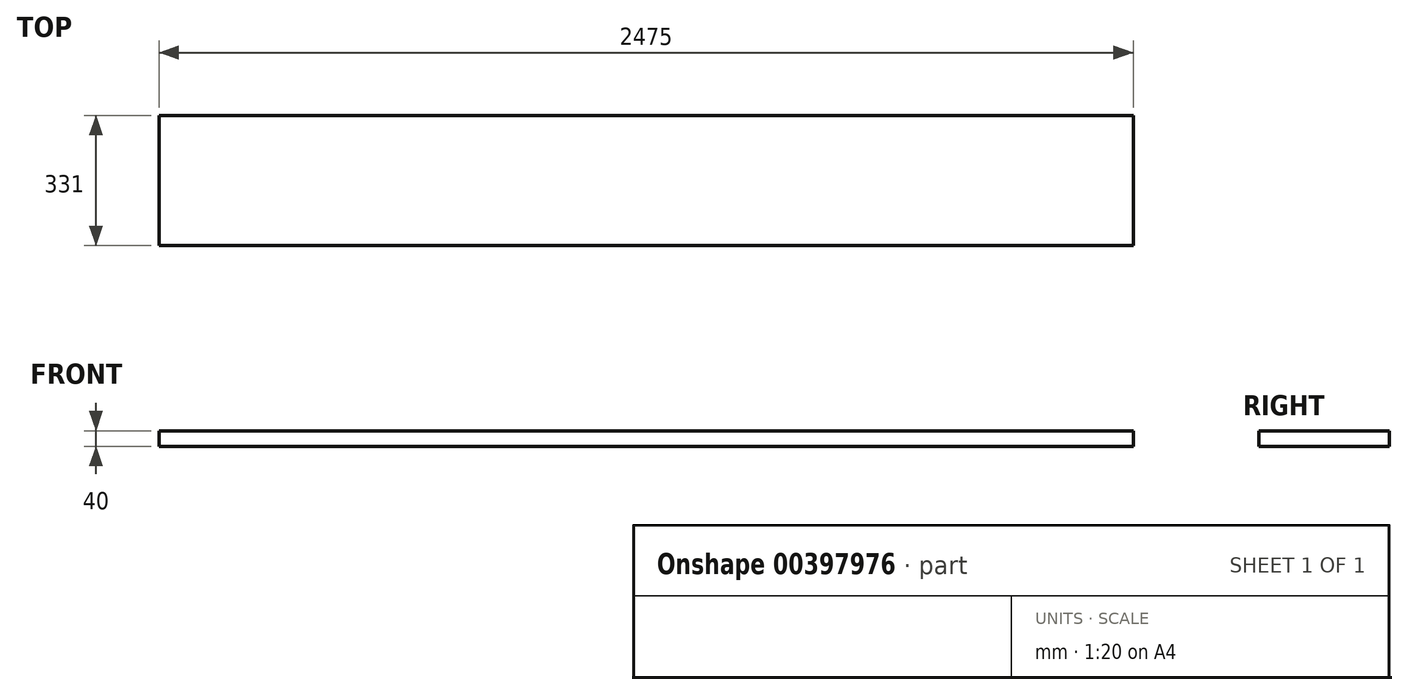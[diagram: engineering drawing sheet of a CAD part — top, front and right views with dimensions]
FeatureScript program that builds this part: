
annotation { "Feature Type Name" : "Feature", "Feature Type Description" : "" }
export const myFeature = defineFeature(function(context is Context, id is Id, definition is map)
    precondition{}
    {
        {
            var Q0;
            Q0=qCreatedBy(makeId("Front.planeOp"),FACE);
            var sketch = newSketch(context, id + "F0", { "sketchPlane" : qUnion([Q0])});
            skLineSegment(sketch, "E0.bottom", {"start": v(-1237.5, 20) * mm, "end": v(1237.5, 20) * mm});
            skLineSegment(sketch, "E0.top", {"start": v(-1237.5, -20) * mm, "end": v(1237.5, -20) * mm});
            skLineSegment(sketch, "E0.left", {"start": v(-1237.5, 20) * mm, "end": v(-1237.5, -20) * mm});
            skLineSegment(sketch, "E0.right", {"start": v(1237.5, 20) * mm, "end": v(1237.5, -20) * mm});
            skLineSegment(sketch, "E1", {"start": v(0, 20) * mm, "end": v(0, -20) * mm, "construction": true});
            skSolve(sketch);
        }
        {
            var Q0;
            Q0 = qSketchRegion(id + "F0", true);
            extrude(context, id + "F1", {"entities" : qUnion([Q0]), "depth" : 331 * mm});
        }
    });
